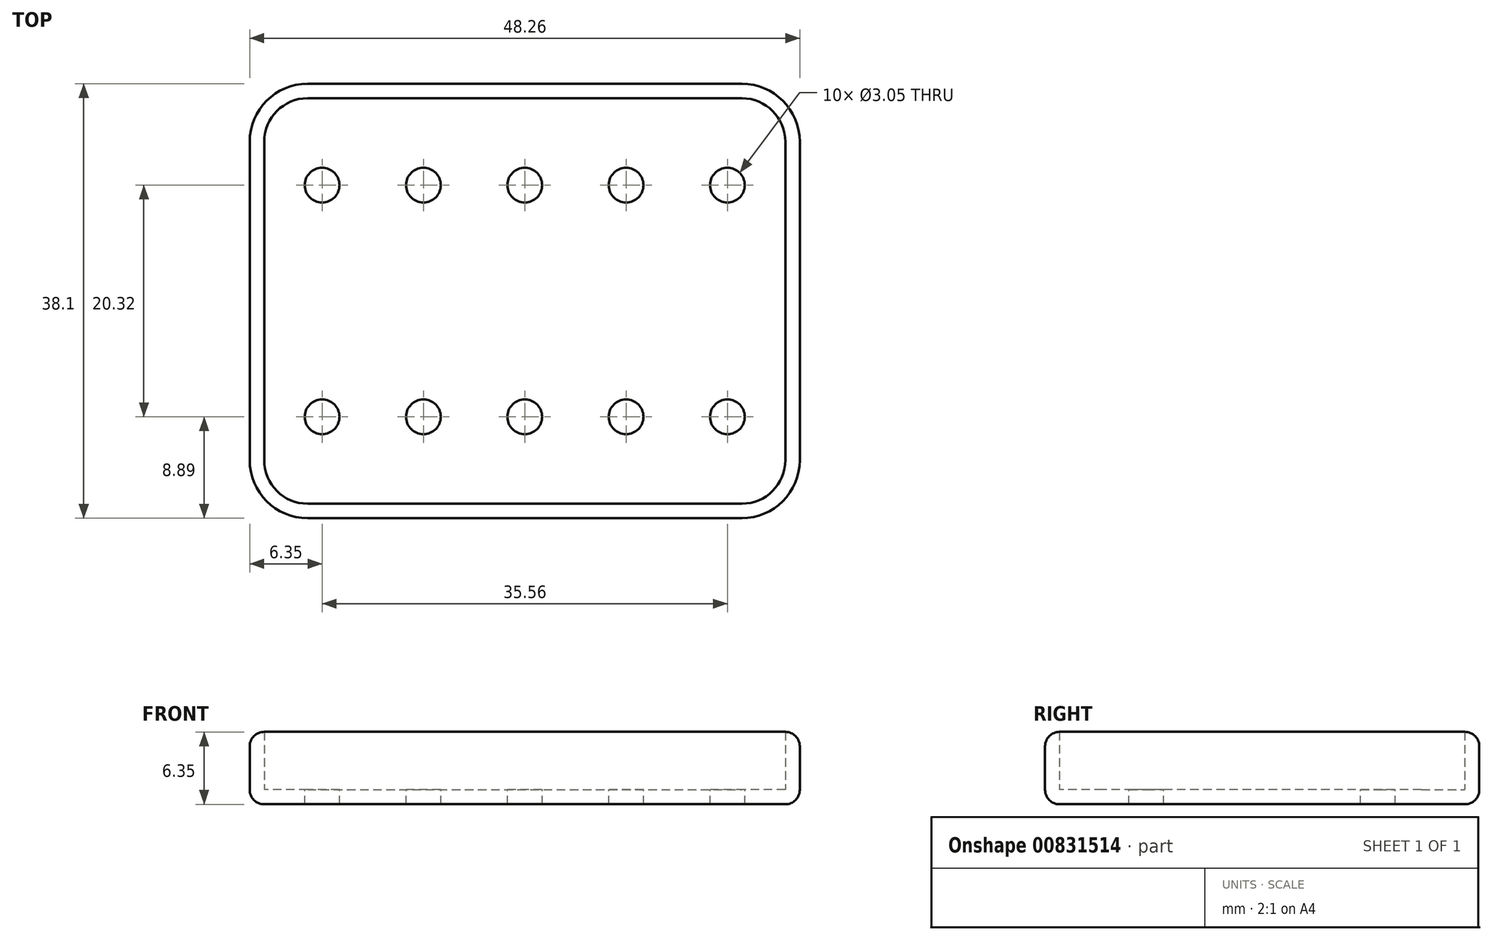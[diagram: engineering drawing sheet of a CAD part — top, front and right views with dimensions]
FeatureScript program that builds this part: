
annotation { "Feature Type Name" : "Feature", "Feature Type Description" : "" }
export const myFeature = defineFeature(function(context is Context, id is Id, definition is map)
    precondition{}
    {
        {
            var Q0;
            Q0=qCreatedBy(makeId("Top.planeOp"),FACE);
            var sketch = newSketch(context, id + "F0", { "sketchPlane" : qUnion([Q0])});
            skLineSegment(sketch, "E0.bottom", {"start": v(19.05, 19.05) * mm, "end": v(-19.05, 19.05) * mm});
            skLineSegment(sketch, "E0.top", {"start": v(19.05, -19.05) * mm, "end": v(-19.05, -19.05) * mm});
            skLineSegment(sketch, "E0.left", {"start": v(24.13, 13.97) * mm, "end": v(24.13, -13.97) * mm});
            skLineSegment(sketch, "E0.right", {"start": v(-24.13, 13.97) * mm, "end": v(-24.13, -13.97) * mm});
            skPoint(sketch, "E0.middle", {"position": v(0, 0) * mm});
            skPoint(sketch, "E1.visualSharp", {"position": v(-24.13, 19.05) * mm});
            skArc(sketch, "E1.filletArc", {"start": v(-19.05, 19.05) * mm, "mid": v(-22.64, 17.56) * mm, "end": v(-24.13, 13.97) * mm});
            skPoint(sketch, "E2.visualSharp", {"position": v(24.13, 19.05) * mm});
            skArc(sketch, "E2.filletArc", {"start": v(24.13, 13.97) * mm, "mid": v(22.64, 17.56) * mm, "end": v(19.05, 19.05) * mm});
            skPoint(sketch, "E3.visualSharp", {"position": v(24.13, -19.05) * mm});
            skArc(sketch, "E3.filletArc", {"start": v(19.05, -19.05) * mm, "mid": v(22.64, -17.56) * mm, "end": v(24.13, -13.97) * mm});
            skPoint(sketch, "E4.visualSharp", {"position": v(-24.13, -19.05) * mm});
            skArc(sketch, "E4.filletArc", {"start": v(-24.13, -13.97) * mm, "mid": v(-22.64, -17.56) * mm, "end": v(-19.05, -19.05) * mm});
            skSolve(sketch);
        }
        {
            var Q0;
            Q0=qCreatedBy(makeId("Top.planeOp"),FACE);
            var sketch = newSketch(context, id + "F1", { "sketchPlane" : qUnion([Q0])});
            skCircle(sketch, "E5", {"center": v(-17.78, 10.16) * mm, "radius": 1.52 * mm});
            skCircle(sketch, "E6", {"center": v(-17.78, -10.16) * mm, "radius": 1.52 * mm});
            skCircle(sketch, "E7.1.0.0", {"center": v(-8.9, 10.16) * mm, "radius": 1.52 * mm});
            skCircle(sketch, "E7.2.0.0", {"center": v(0, 10.16) * mm, "radius": 1.52 * mm});
            skCircle(sketch, "E7.3.0.0", {"center": v(8.89, 10.16) * mm, "radius": 1.52 * mm});
            skCircle(sketch, "E7.4.0.0", {"center": v(17.78, 10.16) * mm, "radius": 1.52 * mm});
            skLineSegment(sketch, "E7.direction1", {"start": v(-17.78, 10.16) * mm, "end": v(-8.9, 10.16) * mm, "construction": true});
            skCircle(sketch, "E8.1.0.0", {"center": v(-8.9, -10.16) * mm, "radius": 1.52 * mm});
            skCircle(sketch, "E8.2.0.0", {"center": v(0, -10.16) * mm, "radius": 1.52 * mm});
            skCircle(sketch, "E8.3.0.0", {"center": v(8.89, -10.16) * mm, "radius": 1.52 * mm});
            skCircle(sketch, "E8.4.0.0", {"center": v(17.78, -10.16) * mm, "radius": 1.52 * mm});
            skLineSegment(sketch, "E8.direction1", {"start": v(-17.78, -10.16) * mm, "end": v(-8.9, -10.16) * mm, "construction": true});
            skSolve(sketch);
        }
        {
            var Q0;
            Q0 = qSketchRegion(id + "F0", true);
            extrude(context, id + "F2", {"entities" : qUnion([Q0]), "endBound" : BoundingType.SYMMETRIC, "depth" : 6.35 * mm, "offsetDistance" : 25.4 * mm});
        }
        {
            var Q0;
            Q0=makeQuery(id+"F2.opExtrude","CAP_EDGE",EDGE,{"disambiguationData":[OSD([sQuery(id+"F0.wireOp",EDGE,"E0.right")])],"isStart":false});
            var Q1;
            Q1=makeQuery(id+"F2.opExtrude","CAP_EDGE",EDGE,{"disambiguationData":[OSD([sQuery(id+"F0.wireOp",EDGE,"E0.right")])],"isStart":true});
            fillet(context, id + "F3", {"entities" : qUnion([Q0, Q1]), "radius" : 1.27 * mm, "tangentPropagation" : true, "allowEdgeOverflow" : false});
        }
        {
            var Q0;
            Q0=makeQuery(id+"F2.opExtrude","CAP_FACE",FACE,{"disambiguationData":[OSD([sQuery(id+"F0.wireOp",EDGE,"E0.bottom"),sQuery(id+"F0.wireOp",EDGE,"E0.top"),sQuery(id+"F0.wireOp",EDGE,"E0.left"),sQuery(id+"F0.wireOp",EDGE,"E0.right"),sQuery(id+"F0.wireOp",EDGE,"E1.filletArc"),sQuery(id+"F0.wireOp",EDGE,"E2.filletArc"),sQuery(id+"F0.wireOp",EDGE,"E3.filletArc"),sQuery(id+"F0.wireOp",EDGE,"E4.filletArc")])],"isStart":false});
            shell(context, id + "F4", {"entities" : qUnion([Q0]), "thickness" : 1.27 * mm});
        }
        {
            var Q0;
            Q0 = qSketchRegion(id + "F1", true);
            extrude(context, id + "F5", {"entities" : qUnion([Q0]), "operationType" : NewBodyOperationType.REMOVE, "oppositeDirection" : true, "depth" : 25.4 * mm, "offsetDistance" : 25.4 * mm});
        }
    });
